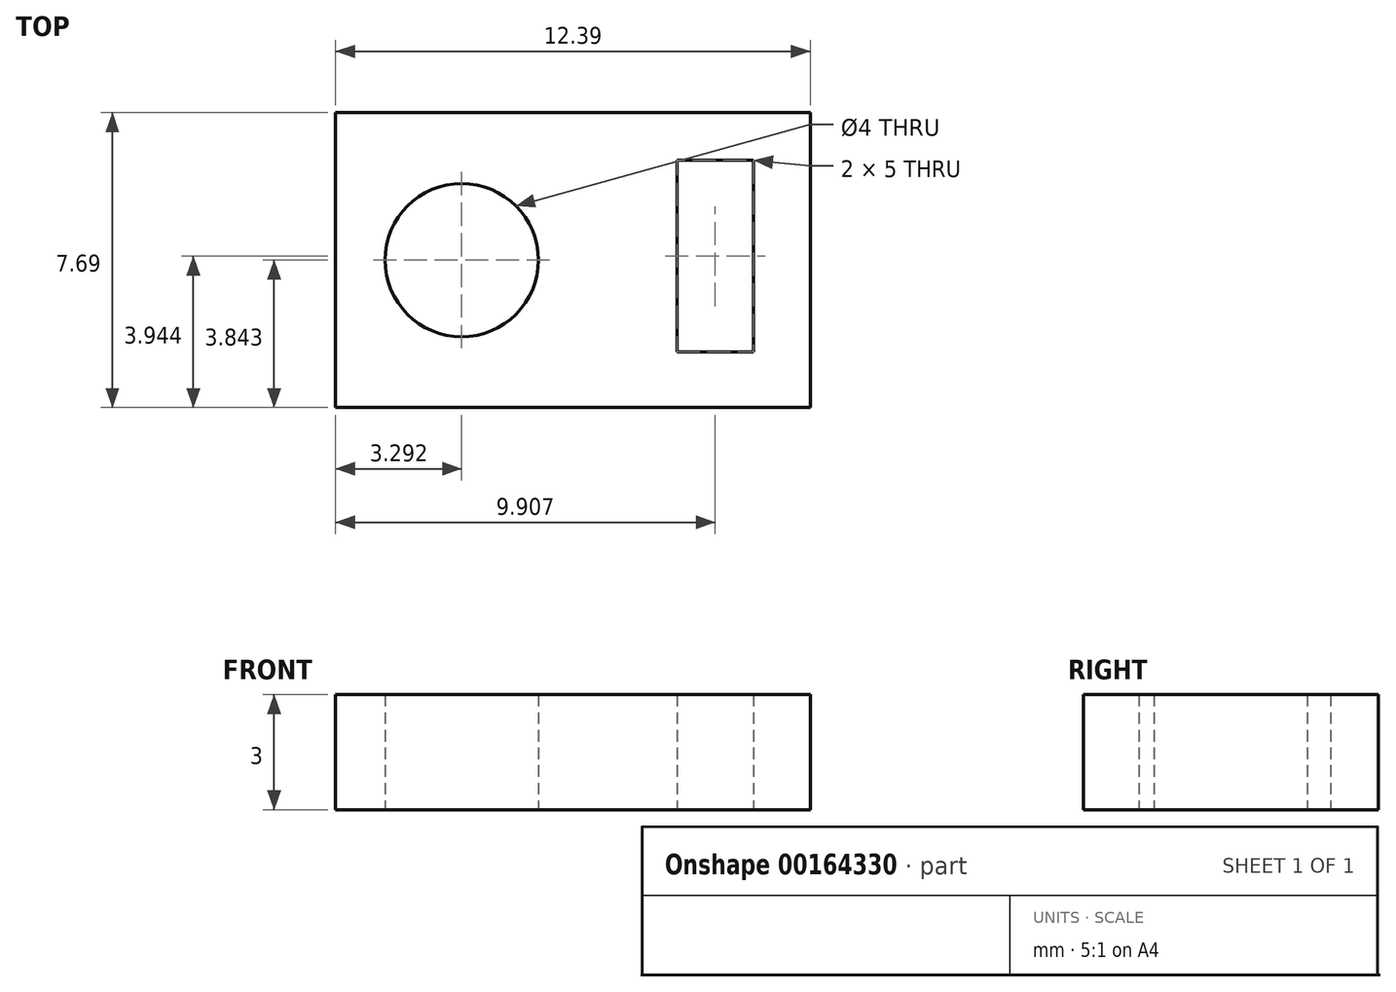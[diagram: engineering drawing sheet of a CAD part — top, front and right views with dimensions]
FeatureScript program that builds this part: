
annotation { "Feature Type Name" : "Feature", "Feature Type Description" : "" }
export const myFeature = defineFeature(function(context is Context, id is Id, definition is map)
    precondition{}
    {
        {
            var Q0;
            Q0=qCreatedBy(makeId("Top.planeOp"),FACE);
            var sketch = newSketch(context, id + "F0", { "sketchPlane" : qUnion([Q0])});
            skLineSegment(sketch, "E0.bottom", {"start": v(-10.14, 9.8) * mm, "end": v(2.25, 9.8) * mm});
            skLineSegment(sketch, "E0.top", {"start": v(-10.14, 2.1) * mm, "end": v(2.25, 2.1) * mm});
            skLineSegment(sketch, "E0.left", {"start": v(-10.14, 9.8) * mm, "end": v(-10.14, 2.1) * mm});
            skLineSegment(sketch, "E0.right", {"start": v(2.25, 9.8) * mm, "end": v(2.25, 2.1) * mm});
            skCircle(sketch, "E1", {"center": v(-6.85, 5.95) * mm, "radius": 2 * mm});
            skPoint(sketch, "E1.centerSnap0", {"position": v(-10.14, 5.95) * mm});
            skLineSegment(sketch, "E2.bottom", {"start": v(-1.23, 8.55) * mm, "end": v(0.77, 8.55) * mm});
            skLineSegment(sketch, "E2.top", {"start": v(-1.23, 3.55) * mm, "end": v(0.77, 3.55) * mm});
            skLineSegment(sketch, "E2.left", {"start": v(-1.23, 8.55) * mm, "end": v(-1.23, 3.55) * mm});
            skLineSegment(sketch, "E2.right", {"start": v(0.77, 8.55) * mm, "end": v(0.77, 3.55) * mm});
            skSolve(sketch);
        }
        {
            var Q0;
            Q0 = qSketchRegion(id + "F0", true);
            extrude(context, id + "F1", {"entities" : qUnion([Q0]), "depth" : 3 * mm});
        }
    });
